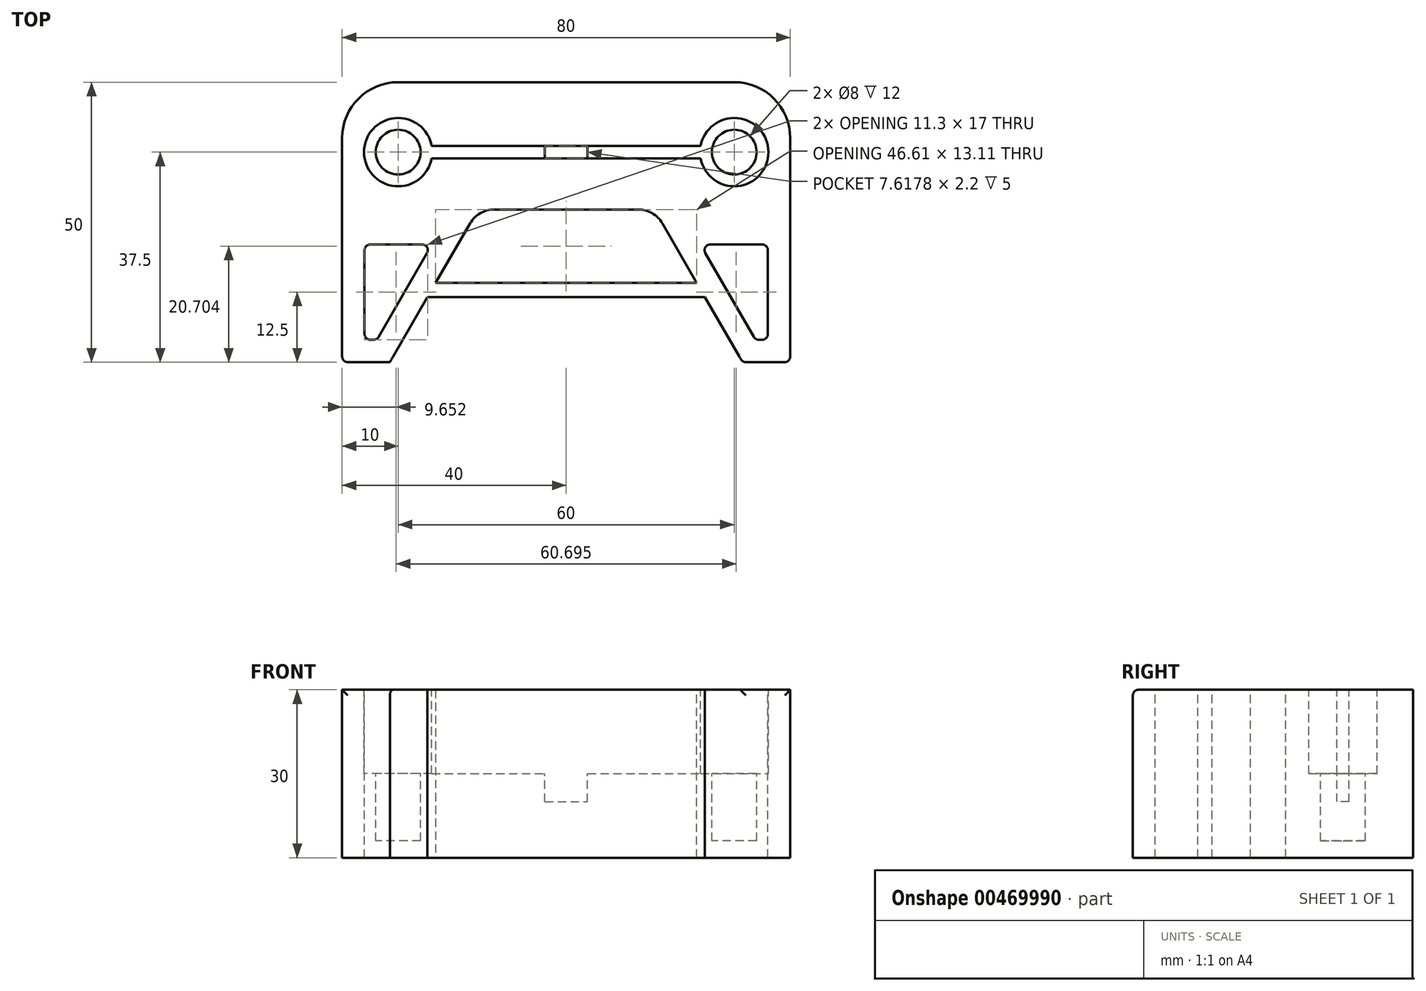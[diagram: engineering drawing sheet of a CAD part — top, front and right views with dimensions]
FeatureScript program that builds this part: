
annotation { "Feature Type Name" : "Feature", "Feature Type Description" : "" }
export const myFeature = defineFeature(function(context is Context, id is Id, definition is map)
    precondition{}
    {
        {
            var Q0;
            Q0=qCreatedBy(makeId("Top.planeOp"),FACE);
            var sketch = newSketch(context, id + "F0", { "sketchPlane" : qUnion([Q0])});
            skLineSegment(sketch, "E0.bottom", {"start": v(-40, 25) * mm, "end": v(40, 25) * mm});
            skLineSegment(sketch, "E0.top", {"start": v(-40, -25) * mm, "end": v(40, -25) * mm});
            skLineSegment(sketch, "E0.left", {"start": v(-40, 25) * mm, "end": v(-40, -25) * mm});
            skLineSegment(sketch, "E0.right", {"start": v(40, 25) * mm, "end": v(40, -25) * mm});
            skPoint(sketch, "E0.middle", {"position": v(0, 0) * mm});
            skSolve(sketch);
        }
        {
            var Q0;
            Q0=makeQuery(id+"F0.imprint","IMPRINT",FACE,{"disambiguationData":[TD([[makeQuery(id+"F0.imprint","IMPRINT",EDGE,{"derivedFrom":sQuery(id+"F0.wireOp",EDGE,"E0.bottom")}),-1.0]])]});
            extrude(context, id + "F1", {"entities" : qUnion([Q0]), "depth" : 30 * mm, "offsetDistance" : 25 * mm});
        }
        {
            var Q0;
            Q0=makeQuery(id+"F1.opExtrude","CAP_FACE",FACE,{"disambiguationData":[OSD([sQuery(id+"F0.wireOp",EDGE,"E0.bottom"),sQuery(id+"F0.wireOp",EDGE,"E0.top"),sQuery(id+"F0.wireOp",EDGE,"E0.left"),sQuery(id+"F0.wireOp",EDGE,"E0.right")])],"isStart":false});
            var sketch = newSketch(context, id + "F2", { "sketchPlane" : qUnion([Q0])});
            skLineSegment(sketch, "E1.bottom", {"start": v(-40, 25) * mm, "end": v(40, 25) * mm, "construction": true});
            skLineSegment(sketch, "E1.top", {"start": v(-40, 0) * mm, "end": v(40, 0) * mm, "construction": true});
            skLineSegment(sketch, "E1.left", {"start": v(-40, 25) * mm, "end": v(-40, 0) * mm, "construction": true});
            skLineSegment(sketch, "E1.right", {"start": v(40, 25) * mm, "end": v(40, 0) * mm, "construction": true});
            skLineSegment(sketch, "E2", {"start": v(0, 0) * mm, "end": v(0, 25) * mm, "construction": true});
            skLineSegment(sketch, "E3.bottom", {"start": v(-30, 19.18) * mm, "end": v(30, 19.18) * mm, "construction": true});
            skLineSegment(sketch, "E3.top", {"start": v(-30, 5.82) * mm, "end": v(30, 5.82) * mm, "construction": true});
            skLineSegment(sketch, "E3.left", {"start": v(-30, 19.18) * mm, "end": v(-30, 5.82) * mm, "construction": true});
            skLineSegment(sketch, "E3.right", {"start": v(30, 19.18) * mm, "end": v(30, 5.82) * mm, "construction": true});
            skPoint(sketch, "E3.middle", {"position": v(0, 12.5) * mm});
            skCircle(sketch, "E4", {"center": v(-30, 12.5) * mm, "radius": 4.1 * mm});
            skCircle(sketch, "E5", {"center": v(30, 12.5) * mm, "radius": 4.1 * mm});
            skLineSegment(sketch, "E6", {"start": v(-30, 12.5) * mm, "end": v(30, 12.5) * mm, "construction": true});
            skLineSegment(sketch, "E7.bottom", {"start": v(-30, 13.6) * mm, "end": v(30, 13.6) * mm, "construction": true});
            skLineSegment(sketch, "E7.top", {"start": v(-30, 11.4) * mm, "end": v(30, 11.4) * mm, "construction": true});
            skLineSegment(sketch, "E7.left", {"start": v(-30, 13.6) * mm, "end": v(-30, 11.4) * mm, "construction": true});
            skLineSegment(sketch, "E7.right", {"start": v(30, 13.6) * mm, "end": v(30, 11.4) * mm, "construction": true});
            skCircle(sketch, "E8.0", {"center": v(-30, 12.5) * mm, "radius": 6.1 * mm});
            skCircle(sketch, "E9.0", {"center": v(30, 12.5) * mm, "radius": 6.1 * mm});
            skLineSegment(sketch, "E10.bottom", {"start": v(-30, 13.6) * mm, "end": v(30, 13.6) * mm});
            skLineSegment(sketch, "E10.top", {"start": v(-30, 11.4) * mm, "end": v(30, 11.4) * mm});
            skLineSegment(sketch, "E10.left", {"start": v(-30, 13.6) * mm, "end": v(-30, 11.4) * mm});
            skLineSegment(sketch, "E10.right", {"start": v(30, 13.6) * mm, "end": v(30, 11.4) * mm});
            skLineSegment(sketch, "E11.bottom", {"start": v(-3.8, 13.6) * mm, "end": v(3.8, 13.6) * mm});
            skLineSegment(sketch, "E11.top", {"start": v(-3.8, 11.4) * mm, "end": v(3.8, 11.4) * mm});
            skLineSegment(sketch, "E11.left", {"start": v(-3.8, 13.6) * mm, "end": v(-3.8, 11.4) * mm});
            skLineSegment(sketch, "E11.right", {"start": v(3.8, 13.6) * mm, "end": v(3.8, 11.4) * mm});
            skSolve(sketch);
        }
        {
            var Q0;
            {var subQ0=sQuery(id+"F2.wireOp",EDGE,"E10.bottom");var subQ1=sQuery(id+"F2.wireOp",EDGE,"E4");var subQ2=makeQuery(id+"F2.imprint","INTERSECT",VERTEX,{"derivedFrom":[subQ1,subQ0]});Q0=makeQuery(id+"F2.imprint","IMPRINT",FACE,{"disambiguationData":[TD([[makeQuery(id+"F2.imprint","IMPRINT",EDGE,{"disambiguationData":[TD([[subQ2,-1.0]])],"derivedFrom":subQ1}),-1.0]])]});}
            var Q1;
            {var subQ0=sQuery(id+"F2.wireOp",EDGE,"E10.bottom");var subQ1=sQuery(id+"F2.wireOp",EDGE,"E4");var subQ2=makeQuery(id+"F2.imprint","INTERSECT",VERTEX,{"derivedFrom":[subQ1,subQ0]});Q1=makeQuery(id+"F2.imprint","IMPRINT",FACE,{"disambiguationData":[TD([[makeQuery(id+"F2.imprint","IMPRINT",EDGE,{"disambiguationData":[TD([[subQ2,1.0]])],"derivedFrom":subQ1}),-1.0]])]});}
            var Q2;
            {var subQ5=sQuery(id+"F2.wireOp",EDGE,"E10.left");Q2=makeQuery(id+"F2.imprint","IMPRINT",FACE,{"disambiguationData":[TD([[makeQuery(id+"F2.imprint","IMPRINT",EDGE,{"derivedFrom":subQ5}),-1.0]])]});}
            var Q3;
            {var subQ5=sQuery(id+"F2.wireOp",EDGE,"E10.left");Q3=makeQuery(id+"F2.imprint","IMPRINT",FACE,{"disambiguationData":[TD([[makeQuery(id+"F2.imprint","IMPRINT",EDGE,{"derivedFrom":subQ5}),1.0]])]});}
            var Q4;
            {var subQ0=sQuery(id+"F2.wireOp",EDGE,"E10.bottom");var subQ1=sQuery(id+"F2.wireOp",EDGE,"E8.0");var subQ2=makeQuery(id+"F2.imprint","INTERSECT",VERTEX,{"derivedFrom":[subQ1,subQ0]});Q4=makeQuery(id+"F2.imprint","IMPRINT",FACE,{"disambiguationData":[TD([[makeQuery(id+"F2.imprint","IMPRINT",EDGE,{"disambiguationData":[TD([[subQ2,1.0]])],"derivedFrom":subQ1}),-1.0]])]});}
            var Q5;
            {var subQ0=sQuery(id+"F2.wireOp",EDGE,"E10.bottom");var subQ1=sQuery(id+"F2.wireOp",EDGE,"E5");var subQ2=makeQuery(id+"F2.imprint","INTERSECT",VERTEX,{"derivedFrom":[subQ1,subQ0]});Q5=makeQuery(id+"F2.imprint","IMPRINT",FACE,{"disambiguationData":[TD([[makeQuery(id+"F2.imprint","IMPRINT",EDGE,{"disambiguationData":[TD([[subQ2,1.0]])],"derivedFrom":subQ1}),-1.0]])]});}
            var Q6;
            {var subQ0=sQuery(id+"F2.wireOp",EDGE,"E10.bottom");var subQ1=sQuery(id+"F2.wireOp",EDGE,"E5");var subQ2=makeQuery(id+"F2.imprint","INTERSECT",VERTEX,{"derivedFrom":[subQ1,subQ0]});Q6=makeQuery(id+"F2.imprint","IMPRINT",FACE,{"disambiguationData":[TD([[makeQuery(id+"F2.imprint","IMPRINT",EDGE,{"disambiguationData":[TD([[subQ2,-1.0]])],"derivedFrom":subQ1}),-1.0]])]});}
            var Q7;
            {var subQ5=sQuery(id+"F2.wireOp",EDGE,"E10.right");Q7=makeQuery(id+"F2.imprint","IMPRINT",FACE,{"disambiguationData":[TD([[makeQuery(id+"F2.imprint","IMPRINT",EDGE,{"derivedFrom":subQ5}),-1.0]])]});}
            var Q8;
            {var subQ5=sQuery(id+"F2.wireOp",EDGE,"E10.right");Q8=makeQuery(id+"F2.imprint","IMPRINT",FACE,{"disambiguationData":[TD([[makeQuery(id+"F2.imprint","IMPRINT",EDGE,{"derivedFrom":subQ5}),1.0]])]});}
            var Q9;
            {var subQ5=sQuery(id+"F2.wireOp",EDGE,"E11.right");Q9=makeQuery(id+"F2.imprint","IMPRINT",FACE,{"disambiguationData":[TD([[makeQuery(id+"F2.imprint","IMPRINT",EDGE,{"derivedFrom":subQ5}),1.0]])]});}
            extrude(context, id + "F3", {"entities" : qUnion([Q0, Q1, Q2, Q3, Q4, Q5, Q6, Q7, Q8, Q9]), "operationType" : NewBodyOperationType.REMOVE, "oppositeDirection" : true, "depth" : 15 * mm, "offsetDistance" : 25 * mm});
        }
        {
            var Q0;
            Q0=makeQuery(id+"F3.boolean.opBoolean","COPY",FACE,{"derivedFrom":makeQuery(id+"F3.opExtrude","CAP_FACE",FACE,{"disambiguationData":[OSD([sQuery(id+"F2.wireOp",EDGE,"E8.0"),sQuery(id+"F2.wireOp",EDGE,"E9.0"),sQuery(id+"F2.wireOp",EDGE,"E10.bottom"),sQuery(id+"F2.wireOp",EDGE,"E10.top")])],"isStart":false})});
            var sketch = newSketch(context, id + "F4", { "sketchPlane" : qUnion([Q0])});
            skCircle(sketch, "E12", {"center": v(-30, 12.5) * mm, "radius": 4 * mm});
            skCircle(sketch, "E13", {"center": v(30, 12.5) * mm, "radius": 4 * mm});
            skSolve(sketch);
        }
        {
            var Q0;
            Q0=makeQuery(id+"F4.imprint","IMPRINT",FACE,{"disambiguationData":[TD([[makeQuery(id+"F4.imprint","IMPRINT",EDGE,{"derivedFrom":sQuery(id+"F4.wireOp",EDGE,"E12")}),1.0]])]});
            var Q1;
            Q1=makeQuery(id+"F4.imprint","IMPRINT",FACE,{"disambiguationData":[TD([[makeQuery(id+"F4.imprint","IMPRINT",EDGE,{"derivedFrom":sQuery(id+"F4.wireOp",EDGE,"E13")}),1.0]])]});
            extrude(context, id + "F5", {"entities" : qUnion([Q0, Q1]), "operationType" : NewBodyOperationType.REMOVE, "oppositeDirection" : true, "depth" : 12 * mm, "offsetDistance" : 25 * mm});
        }
        {
            var Q0;
            Q0=makeQuery(id+"F1.opExtrude","SWEPT_EDGE",EDGE,{"disambiguationData":[OSD([sQuery(id+"F0.wireOp",EDGE,"E0.bottom"),sQuery(id+"F0.wireOp",EDGE,"E0.left")])]});
            var Q1;
            Q1=makeQuery(id+"F1.opExtrude","SWEPT_EDGE",EDGE,{"disambiguationData":[OSD([sQuery(id+"F0.wireOp",EDGE,"E0.bottom"),sQuery(id+"F0.wireOp",EDGE,"E0.right")])]});
            fillet(context, id + "F6", {"entities" : qUnion([Q0, Q1]), "radius" : 10 * mm, "tangentPropagation" : true, "allowEdgeOverflow" : false});
        }
        {
            var Q0;
            Q0=makeQuery(id+"F1.opExtrude","CAP_FACE",FACE,{"disambiguationData":[OSD([sQuery(id+"F0.wireOp",EDGE,"E0.bottom"),sQuery(id+"F0.wireOp",EDGE,"E0.top"),sQuery(id+"F0.wireOp",EDGE,"E0.left"),sQuery(id+"F0.wireOp",EDGE,"E0.right")])],"isStart":false});
            var sketch = newSketch(context, id + "F7", { "sketchPlane" : qUnion([Q0])});
            skCircle(sketch, "E14.cCircle", {"center": v(0, -25) * mm, "radius": 27.26 * mm, "construction": true});
            skPoint(sketch, "E14.cCircle.perimeterSnap0", {"position": v(0, -25) * mm});
            skLineSegment(sketch, "E14.0", {"start": v(-15.74, 2.26) * mm, "end": v(15.74, 2.26) * mm});
            skLineSegment(sketch, "E14.1", {"start": v(15.74, 2.26) * mm, "end": v(31.48, -25) * mm});
            skLineSegment(sketch, "E14.2", {"start": v(31.48, -25) * mm, "end": v(15.74, -52.26) * mm});
            skLineSegment(sketch, "E14.3", {"start": v(15.74, -52.26) * mm, "end": v(-15.74, -52.26) * mm});
            skLineSegment(sketch, "E14.4", {"start": v(-15.74, -52.26) * mm, "end": v(-31.48, -25) * mm});
            skLineSegment(sketch, "E14.5", {"start": v(-31.48, -25) * mm, "end": v(-15.74, 2.26) * mm});
            skPoint(sketch, "E14.0.midPoint", {"position": v(0, 2.26) * mm});
            skPoint(sketch, "E14.0.midPoint.positionSnap0", {"position": v(0, -25) * mm});
            skSolve(sketch);
        }
        {
            var Q0;
            Q0=makeQuery(id+"F7.imprint","IMPRINT",FACE,{"disambiguationData":[TD([[makeQuery(id+"F7.imprint","IMPRINT",EDGE,{"derivedFrom":sQuery(id+"F7.wireOp",EDGE,"E14.0")}),-1.0]])]});
            extrude(context, id + "F8", {"entities" : qUnion([Q0]), "operationType" : NewBodyOperationType.REMOVE, "oppositeDirection" : true, "depth" : 30 * mm, "offsetDistance" : 25 * mm});
        }
        {
            var Q0;
            Q0=makeQuery(id+"F8.boolean.opBoolean","COPY",EDGE,{"derivedFrom":makeQuery(id+"F8.opExtrude","SWEPT_EDGE",EDGE,{"disambiguationData":[OSD([sQuery(id+"F7.wireOp",EDGE,"E14.0"),sQuery(id+"F7.wireOp",EDGE,"E14.1")])]})});
            var Q1;
            Q1=makeQuery(id+"F8.boolean.opBoolean","COPY",EDGE,{"derivedFrom":makeQuery(id+"F8.opExtrude","SWEPT_EDGE",EDGE,{"disambiguationData":[OSD([sQuery(id+"F7.wireOp",EDGE,"E14.0"),sQuery(id+"F7.wireOp",EDGE,"E14.5")])]})});
            fillet(context, id + "F9", {"entities" : qUnion([Q0, Q1]), "radius" : 5 * mm, "tangentPropagation" : true, "allowEdgeOverflow" : false});
        }
        {
            var Q0;
            Q0=makeQuery(id+"F1.opExtrude","CAP_FACE",FACE,{"disambiguationData":[OSD([sQuery(id+"F0.wireOp",EDGE,"E0.bottom"),sQuery(id+"F0.wireOp",EDGE,"E0.top"),sQuery(id+"F0.wireOp",EDGE,"E0.left"),sQuery(id+"F0.wireOp",EDGE,"E0.right")])],"isStart":false});
            var sketch = newSketch(context, id + "F10", { "sketchPlane" : qUnion([Q0])});
            skLineSegment(sketch, "E15", {"start": v(-40, 0) * mm, "end": v(-17.03, 0) * mm});
            skLineSegment(sketch, "E16", {"start": v(-17.03, 0) * mm, "end": v(-31.48, -25) * mm});
            skLineSegment(sketch, "E17", {"start": v(-31.48, -25) * mm, "end": v(-40, -25) * mm});
            skLineSegment(sketch, "E18", {"start": v(-40, -25) * mm, "end": v(-40, 0) * mm});
            skLineSegment(sketch, "E19.0", {"start": v(-36, -4) * mm, "end": v(-23.96, -4) * mm});
            skLineSegment(sketch, "E19.1", {"start": v(-36, -21) * mm, "end": v(-36, -4) * mm});
            skLineSegment(sketch, "E19.2", {"start": v(-33.78, -21) * mm, "end": v(-36, -21) * mm});
            skLineSegment(sketch, "E19.3", {"start": v(-23.96, -4) * mm, "end": v(-33.78, -21) * mm});
            skLineSegment(sketch, "E20.MirrorCS", {"start": v(23.96, -4) * mm, "end": v(33.78, -21) * mm});
            skLineSegment(sketch, "E21.MirrorCS", {"start": v(33.78, -21) * mm, "end": v(36, -21) * mm});
            skLineSegment(sketch, "E22.MirrorCS", {"start": v(36, -21) * mm, "end": v(36, -4) * mm});
            skLineSegment(sketch, "E23.MirrorCS", {"start": v(36, -4) * mm, "end": v(23.96, -4) * mm});
            skSolve(sketch);
        }
        {
            var Q0;
            Q0=makeQuery(id+"F10.imprint","IMPRINT",FACE,{"disambiguationData":[TD([[makeQuery(id+"F10.imprint","IMPRINT",EDGE,{"derivedFrom":sQuery(id+"F10.wireOp",EDGE,"E19.0")}),-1.0]])]});
            var Q1;
            Q1=makeQuery(id+"F10.imprint","IMPRINT",FACE,{"disambiguationData":[TD([[makeQuery(id+"F10.imprint","IMPRINT",EDGE,{"derivedFrom":sQuery(id+"F10.wireOp",EDGE,"E20.MirrorCS")}),1.0]])]});
            extrude(context, id + "F11", {"entities" : qUnion([Q0, Q1]), "operationType" : NewBodyOperationType.REMOVE, "oppositeDirection" : true, "depth" : 32 * mm, "offsetDistance" : 25 * mm});
        }
        {
            var Q0;
            Q0=makeQuery(id+"F11.boolean.opBoolean","COPY",EDGE,{"derivedFrom":makeQuery(id+"F11.opExtrude","SWEPT_EDGE",EDGE,{"disambiguationData":[OSD([sQuery(id+"F10.wireOp",EDGE,"E19.0"),sQuery(id+"F10.wireOp",EDGE,"E19.3")])]})});
            var Q1;
            Q1=makeQuery(id+"F11.boolean.opBoolean","COPY",EDGE,{"derivedFrom":makeQuery(id+"F11.opExtrude","SWEPT_EDGE",EDGE,{"disambiguationData":[OSD([sQuery(id+"F10.wireOp",EDGE,"E19.1"),sQuery(id+"F10.wireOp",EDGE,"E19.2")])]})});
            var Q2;
            Q2=makeQuery(id+"F11.boolean.opBoolean","COPY",EDGE,{"derivedFrom":makeQuery(id+"F11.opExtrude","SWEPT_EDGE",EDGE,{"disambiguationData":[OSD([sQuery(id+"F10.wireOp",EDGE,"E19.0"),sQuery(id+"F10.wireOp",EDGE,"E19.1")])]})});
            var Q3;
            Q3=makeQuery(id+"F11.boolean.opBoolean","COPY",EDGE,{"derivedFrom":makeQuery(id+"F11.opExtrude","SWEPT_EDGE",EDGE,{"disambiguationData":[OSD([sQuery(id+"F10.wireOp",EDGE,"E19.2"),sQuery(id+"F10.wireOp",EDGE,"E19.3")])]})});
            var Q4;
            Q4=makeQuery(id+"F11.boolean.opBoolean","COPY",EDGE,{"derivedFrom":makeQuery(id+"F11.opExtrude","SWEPT_EDGE",EDGE,{"disambiguationData":[OSD([sQuery(id+"F10.wireOp",EDGE,"E20.MirrorCS"),sQuery(id+"F10.wireOp",EDGE,"E23.MirrorCS")])]})});
            var Q5;
            Q5=makeQuery(id+"F11.boolean.opBoolean","COPY",EDGE,{"derivedFrom":makeQuery(id+"F11.opExtrude","SWEPT_EDGE",EDGE,{"disambiguationData":[OSD([sQuery(id+"F10.wireOp",EDGE,"E22.MirrorCS"),sQuery(id+"F10.wireOp",EDGE,"E23.MirrorCS")])]})});
            var Q6;
            Q6=makeQuery(id+"F11.boolean.opBoolean","COPY",EDGE,{"derivedFrom":makeQuery(id+"F11.opExtrude","SWEPT_EDGE",EDGE,{"disambiguationData":[OSD([sQuery(id+"F10.wireOp",EDGE,"E21.MirrorCS"),sQuery(id+"F10.wireOp",EDGE,"E22.MirrorCS")])]})});
            var Q7;
            Q7=makeQuery(id+"F11.boolean.opBoolean","COPY",EDGE,{"derivedFrom":makeQuery(id+"F11.opExtrude","SWEPT_EDGE",EDGE,{"disambiguationData":[OSD([sQuery(id+"F10.wireOp",EDGE,"E20.MirrorCS"),sQuery(id+"F10.wireOp",EDGE,"E21.MirrorCS")])]})});
            fillet(context, id + "F12", {"entities" : qUnion([Q0, Q1, Q2, Q3, Q4, Q5, Q6, Q7]), "radius" : 1 * mm, "tangentPropagation" : true, "allowEdgeOverflow" : false});
        }
        {
            var Q0;
            {var subQ0=sQuery(id+"F0.wireOp",EDGE,"E0.left");var subQ1=sQuery(id+"F0.wireOp",EDGE,"E0.top");Q0=makeQuery(id+"F8.boolean.opBoolean","SPLIT",EDGE,{"disambiguationData":[TD([makeQuery(id+"F1.opExtrude","SWEPT_FACE",FACE,{"disambiguationData":[OSD([subQ0])]})])],"derivedFrom":makeQuery(id+"F1.opExtrude","CAP_EDGE",EDGE,{"disambiguationData":[OSD([subQ1])],"isStart":false})});}
            var Q1;
            {var subQ0=sQuery(id+"F0.wireOp",EDGE,"E0.right");var subQ1=sQuery(id+"F0.wireOp",EDGE,"E0.top");Q1=makeQuery(id+"F8.boolean.opBoolean","SPLIT",EDGE,{"disambiguationData":[TD([makeQuery(id+"F1.opExtrude","SWEPT_FACE",FACE,{"disambiguationData":[OSD([subQ0])]})])],"derivedFrom":makeQuery(id+"F1.opExtrude","CAP_EDGE",EDGE,{"disambiguationData":[OSD([subQ1])],"isStart":false})});}
            var Q2;
            Q2=makeQuery(id+"F1.opExtrude","SWEPT_EDGE",EDGE,{"disambiguationData":[OSD([sQuery(id+"F0.wireOp",EDGE,"E0.top"),sQuery(id+"F0.wireOp",EDGE,"E0.left")])]});
            var Q3;
            Q3=makeQuery(id+"F8.boolean.opBoolean","COPY",EDGE,{"derivedFrom":makeQuery(id+"F8.opExtrude","SWEPT_EDGE",EDGE,{"disambiguationData":[OSD([sQuery(id+"F0.wireOp",EDGE,"E0.top"),sQuery(id+"F7.wireOp",EDGE,"E14.4"),sQuery(id+"F7.wireOp",EDGE,"E14.5")])]})});
            var Q4;
            Q4=makeQuery(id+"F8.boolean.opBoolean","COPY",EDGE,{"derivedFrom":makeQuery(id+"F8.opExtrude","SWEPT_EDGE",EDGE,{"disambiguationData":[OSD([sQuery(id+"F0.wireOp",EDGE,"E0.top"),sQuery(id+"F7.wireOp",EDGE,"E14.1"),sQuery(id+"F7.wireOp",EDGE,"E14.2")])]})});
            var Q5;
            Q5=makeQuery(id+"F1.opExtrude","SWEPT_EDGE",EDGE,{"disambiguationData":[OSD([sQuery(id+"F0.wireOp",EDGE,"E0.top"),sQuery(id+"F0.wireOp",EDGE,"E0.right")])]});
            fillet(context, id + "F13", {"entities" : qUnion([Q0, Q1, Q2, Q3, Q4, Q5]), "radius" : 1 * mm, "tangentPropagation" : true, "allowEdgeOverflow" : false});
        }
        {
            var Q0;
            Q0=makeQuery(id+"F1.opExtrude","CAP_FACE",FACE,{"disambiguationData":[OSD([sQuery(id+"F0.wireOp",EDGE,"E0.bottom"),sQuery(id+"F0.wireOp",EDGE,"E0.top"),sQuery(id+"F0.wireOp",EDGE,"E0.left"),sQuery(id+"F0.wireOp",EDGE,"E0.right")])],"isStart":false});
            var sketch = newSketch(context, id + "F14", { "sketchPlane" : qUnion([Q0])});
            skLineSegment(sketch, "E24.bottom", {"start": v(-4.59, 13.6) * mm, "end": v(6.05, 13.6) * mm, "construction": true});
            skLineSegment(sketch, "E24.top", {"start": v(-4.59, 11.4) * mm, "end": v(6.05, 11.4) * mm, "construction": true});
            skLineSegment(sketch, "E24.left", {"start": v(-4.59, 13.6) * mm, "end": v(-4.59, 11.4) * mm, "construction": true});
            skLineSegment(sketch, "E24.right", {"start": v(6.05, 13.6) * mm, "end": v(6.05, 11.4) * mm, "construction": true});
            skLineSegment(sketch, "E25.bottom", {"start": v(-3.8, 13.6) * mm, "end": v(3.8, 13.6) * mm, "construction": true});
            skLineSegment(sketch, "E25.top", {"start": v(-3.8, 11.4) * mm, "end": v(3.8, 11.4) * mm, "construction": true});
            skLineSegment(sketch, "E25.left", {"start": v(-3.8, 13.6) * mm, "end": v(-3.8, 11.4) * mm, "construction": true});
            skLineSegment(sketch, "E25.right", {"start": v(3.8, 13.6) * mm, "end": v(3.8, 11.4) * mm, "construction": true});
            skLineSegment(sketch, "E26.bottom", {"start": v(-3.8, 13.6) * mm, "end": v(3.8, 13.6) * mm});
            skLineSegment(sketch, "E26.top", {"start": v(-3.8, 11.4) * mm, "end": v(3.8, 11.4) * mm});
            skLineSegment(sketch, "E26.left", {"start": v(-3.8, 13.6) * mm, "end": v(-3.8, 11.4) * mm});
            skLineSegment(sketch, "E26.right", {"start": v(3.8, 13.6) * mm, "end": v(3.8, 11.4) * mm});
            skSolve(sketch);
        }
        {
            var Q0;
            Q0=makeQuery(id+"F14.imprint","IMPRINT",FACE,{"disambiguationData":[TD([[makeQuery(id+"F14.imprint","IMPRINT",EDGE,{"derivedFrom":sQuery(id+"F14.wireOp",EDGE,"E26.bottom")}),-1.0]])]});
            extrude(context, id + "F15", {"entities" : qUnion([Q0]), "operationType" : NewBodyOperationType.REMOVE, "oppositeDirection" : true, "depth" : 20 * mm, "offsetDistance" : 25 * mm});
        }
        {
            var Q0;
            Q0=makeQuery(id+"F1.opExtrude","CAP_FACE",FACE,{"disambiguationData":[OSD([sQuery(id+"F0.wireOp",EDGE,"E0.bottom"),sQuery(id+"F0.wireOp",EDGE,"E0.top"),sQuery(id+"F0.wireOp",EDGE,"E0.left"),sQuery(id+"F0.wireOp",EDGE,"E0.right")])],"isStart":false});
            var sketch = newSketch(context, id + "F16", { "sketchPlane" : qUnion([Q0])});
            skLineSegment(sketch, "E27.bottom", {"start": v(-25.53, -10.85) * mm, "end": v(25.53, -10.85) * mm});
            skLineSegment(sketch, "E27.top", {"start": v(-25.53, -13.4) * mm, "end": v(25.53, -13.4) * mm});
            skLineSegment(sketch, "E27.left", {"start": v(-25.53, -10.85) * mm, "end": v(-25.53, -13.4) * mm});
            skLineSegment(sketch, "E27.right", {"start": v(25.53, -10.85) * mm, "end": v(25.53, -13.4) * mm});
            skPoint(sketch, "E27.middle", {"position": v(0, -12.12) * mm});
            skPoint(sketch, "E27.middle.positionSnap0", {"position": v(-24.04, -12.12) * mm});
            skPoint(sketch, "E27.centerSnap0", {"position": v(-24.04, -12.12) * mm});
            skSolve(sketch);
        }
        {
            var Q0;
            {var subQ0=sQuery(id+"F16.wireOp",EDGE,"E27.bottom");var subQ1=makeQuery(id+"F8.boolean.opBoolean","COPY",EDGE,{"derivedFrom":makeQuery(id+"F8.opExtrude","CAP_EDGE",EDGE,{"disambiguationData":[OSD([sQuery(id+"F7.wireOp",EDGE,"E14.5")])],"isStart":true})});var subQ2=makeQuery(id+"F16.imprint","INTERSECT",VERTEX,{"derivedFrom":[subQ1,subQ0]});Q0=makeQuery(id+"F16.imprint","IMPRINT",FACE,{"disambiguationData":[TD([[makeQuery(id+"F16.imprint","IMPRINT",EDGE,{"disambiguationData":[TD([[subQ2,-1.0]])],"derivedFrom":subQ0}),-1.0]])]});}
            extrude(context, id + "F17", {"entities" : qUnion([Q0]), "operationType" : NewBodyOperationType.ADD, "oppositeDirection" : true, "depth" : 30 * mm, "offsetDistance" : 25 * mm});
        }
    });
